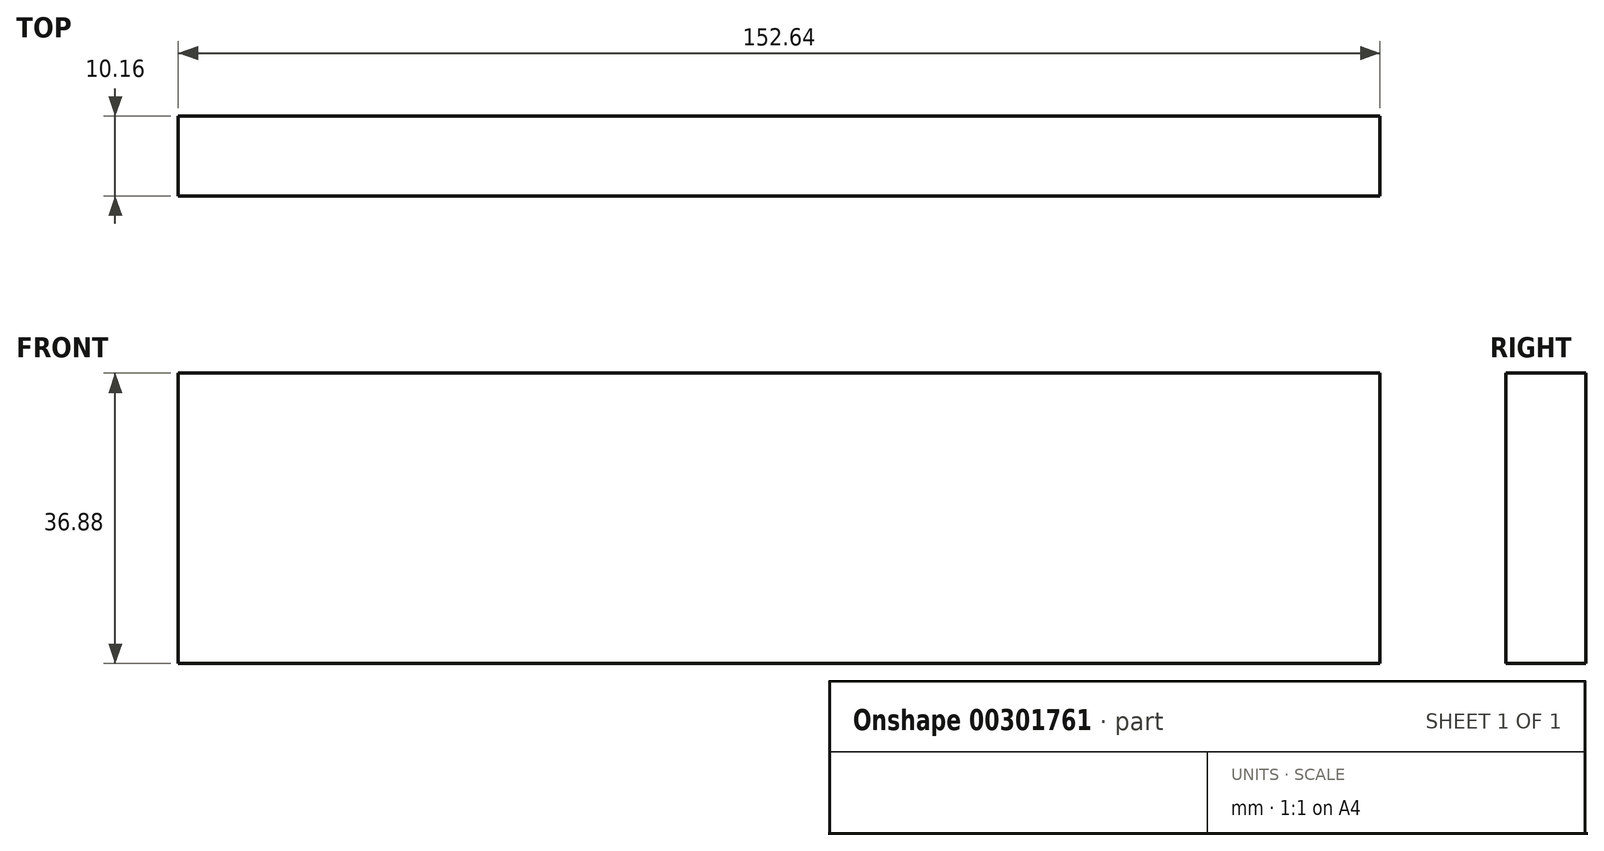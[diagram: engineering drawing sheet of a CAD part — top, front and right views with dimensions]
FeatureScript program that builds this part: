
annotation { "Feature Type Name" : "Feature", "Feature Type Description" : "" }
export const myFeature = defineFeature(function(context is Context, id is Id, definition is map)
    precondition{}
    {
        {
            var Q0;
            Q0=qCreatedBy(makeId("Front.planeOp"),FACE);
            var sketch = newSketch(context, id + "F0", { "sketchPlane" : qUnion([Q0])});
            skLineSegment(sketch, "E0.bottom", {"start": v(76.32, -18.44) * mm, "end": v(-76.32, -18.44) * mm});
            skLineSegment(sketch, "E0.top", {"start": v(76.32, 18.44) * mm, "end": v(-76.32, 18.44) * mm});
            skLineSegment(sketch, "E0.left", {"start": v(76.32, -18.44) * mm, "end": v(76.32, 18.44) * mm});
            skLineSegment(sketch, "E0.right", {"start": v(-76.32, -18.44) * mm, "end": v(-76.32, 18.44) * mm});
            skPoint(sketch, "E0.middle", {"position": v(0, 0) * mm});
            skSolve(sketch);
        }
        {
            var Q0;
            Q0 = qSketchRegion(id + "F0", true);
            extrude(context, id + "F1", {"entities" : qUnion([Q0]), "depth" : 10.16 * mm});
        }
    });
